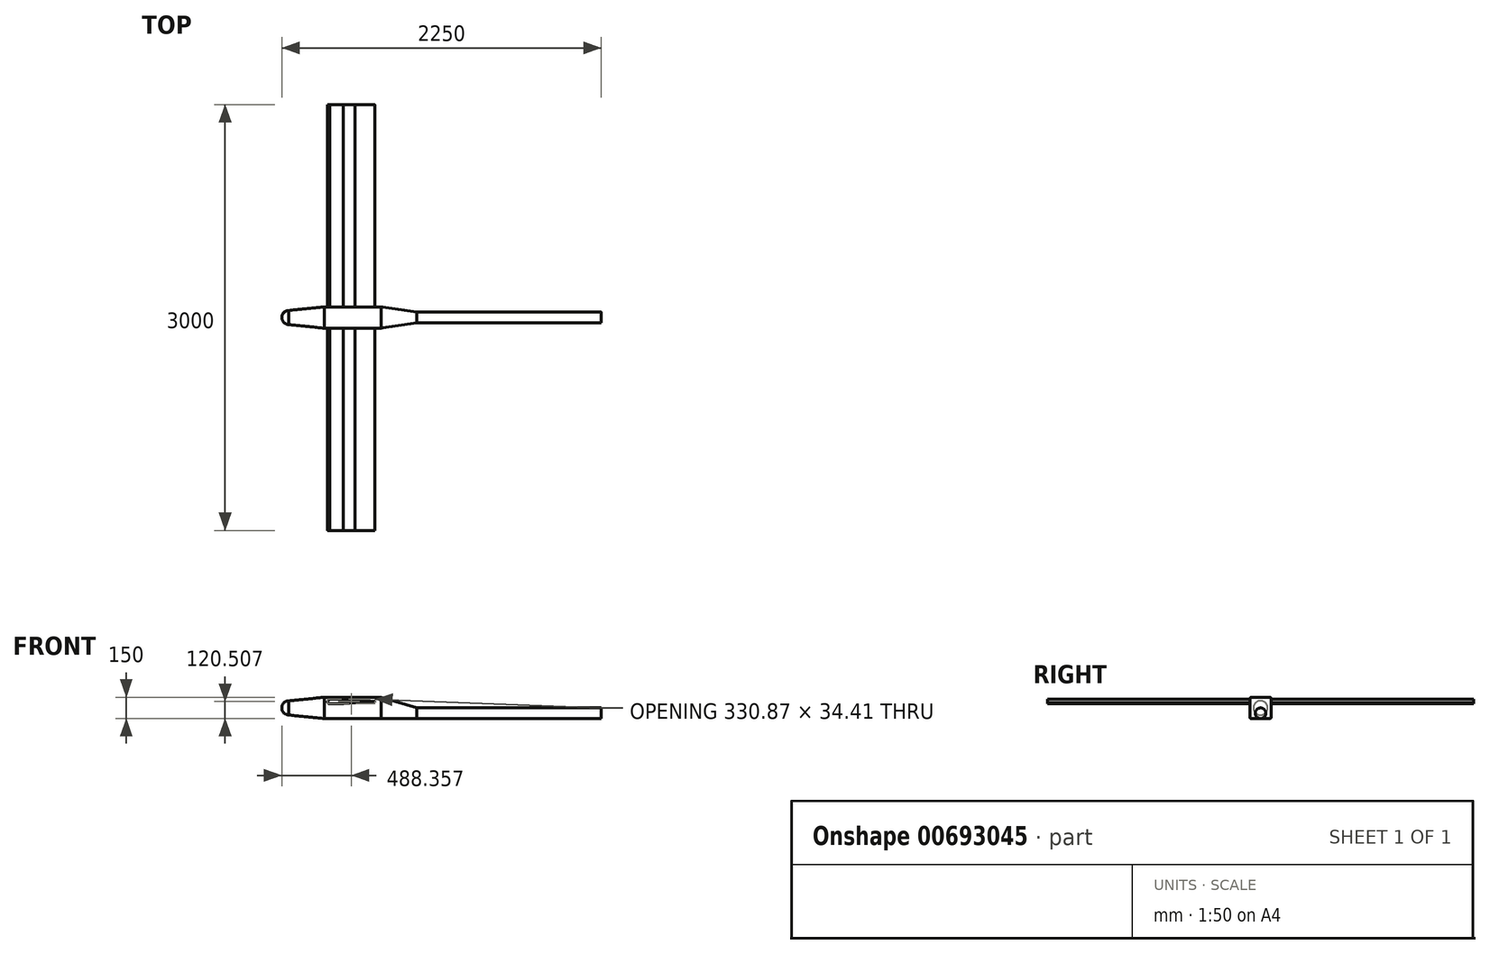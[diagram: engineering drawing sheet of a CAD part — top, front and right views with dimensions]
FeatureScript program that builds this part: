
annotation { "Feature Type Name" : "Feature", "Feature Type Description" : "" }
export const myFeature = defineFeature(function(context is Context, id is Id, definition is map)
    precondition{}
    {
        {
            var Q0;
            Q0=qCreatedBy(makeId("Top.planeOp"),FACE);
            var sketch = newSketch(context, id + "F0", { "sketchPlane" : qUnion([Q0])});
            skLineSegment(sketch, "E0", {"start": v(0, 0) * mm, "end": v(50, 0) * mm, "construction": true});
            skLineSegment(sketch, "E1", {"start": v(0, 0) * mm, "end": v(2000, 0) * mm, "construction": true});
            skCircle(sketch, "E2", {"center": v(50, 0) * mm, "radius": 50 * mm});
            skLineSegment(sketch, "E3", {"start": v(0, 0) * mm, "end": v(300, 0) * mm, "construction": true});
            skLineSegment(sketch, "E4", {"start": v(300, 0) * mm, "end": v(300, -100) * mm, "construction": true});
            skLineSegment(sketch, "E5", {"start": v(300, 0) * mm, "end": v(300, 100) * mm, "construction": true});
            skSolve(sketch);
        }
        {
            var Q0;
            Q0=qCreatedBy(makeId("Right.planeOp"),FACE);
            cPlane(context, id + "F1", {"entities" : qUnion([Q0]), "cplaneType" : CPlaneType.OFFSET, "offset" : 300 * mm, "width" : 152.4 * mm, "height" : 152.4 * mm});
        }
        {
            var Q0;
            Q0=qCreatedBy(makeId("Right.planeOp"),FACE);
            cPlane(context, id + "F2", {"entities" : qUnion([Q0]), "cplaneType" : CPlaneType.OFFSET, "offset" : 50 * mm, "width" : 152.4 * mm, "height" : 152.4 * mm});
        }
        {
            var Q0;
            Q0=qCreatedBy(id+"F2.planeOp",FACE);
            var sketch = newSketch(context, id + "F3", { "sketchPlane" : qUnion([Q0])});
            skCircle(sketch, "E6", {"center": v(0, 0) * mm, "radius": 50 * mm});
            skSolve(sketch);
        }
        {
            var Q0;
            Q0=qCreatedBy(id+"F1.planeOp",FACE);
            var sketch = newSketch(context, id + "F4", { "sketchPlane" : qUnion([Q0])});
            skLineSegment(sketch, "E7.bottom", {"start": v(-65, 75) * mm, "end": v(65, 75) * mm});
            skLineSegment(sketch, "E7.top", {"start": v(-65, -75) * mm, "end": v(65, -75) * mm});
            skLineSegment(sketch, "E7.left", {"start": v(-75, 65) * mm, "end": v(-75, -65) * mm});
            skLineSegment(sketch, "E7.right", {"start": v(75, 65) * mm, "end": v(75, -65) * mm});
            skPoint(sketch, "E7.middle", {"position": v(0, 0) * mm});
            skArc(sketch, "E8", {"start": v(75, 65) * mm, "mid": v(72.07, 72.07) * mm, "end": v(65, 75) * mm});
            skPoint(sketch, "E8.first.point", {"position": v(75, 65) * mm});
            skPoint(sketch, "E8.second.point", {"position": v(65, 75) * mm});
            skPoint(sketch, "E8.third.point", {"position": v(55.59, 61.62) * mm});
            skArc(sketch, "E9", {"start": v(-65, 75) * mm, "mid": v(-72.07, 72.07) * mm, "end": v(-75, 65) * mm});
            skPoint(sketch, "E9.first.point", {"position": v(-65, 75) * mm});
            skPoint(sketch, "E9.second.point", {"position": v(-75, 65) * mm});
            skPoint(sketch, "E9.third.point", {"position": v(-56.26, 60.14) * mm});
            skArc(sketch, "E10", {"start": v(-75, -65) * mm, "mid": v(-72.07, -72.07) * mm, "end": v(-65, -75) * mm});
            skPoint(sketch, "E10.first.point", {"position": v(-75, -65) * mm});
            skPoint(sketch, "E10.second.point", {"position": v(-65, -75) * mm});
            skPoint(sketch, "E10.third.point", {"position": v(-55.94, -69.23) * mm});
            skArc(sketch, "E11", {"start": v(65, -75) * mm, "mid": v(72.07, -72.07) * mm, "end": v(75, -65) * mm});
            skPoint(sketch, "E11.first.point", {"position": v(65, -75) * mm});
            skPoint(sketch, "E11.second.point", {"position": v(75, -65) * mm});
            skPoint(sketch, "E11.third.point", {"position": v(57.58, -58.3) * mm});
            skPoint(sketch, "E12.orphan", {"position": v(75, 75) * mm});
            skPoint(sketch, "E13.orphan", {"position": v(-75, 75) * mm});
            skPoint(sketch, "E14.orphan", {"position": v(75, -75) * mm});
            skPoint(sketch, "E15.orphan", {"position": v(-75, -75) * mm});
            skSolve(sketch);
        }
        {
            var Q0;
            Q0=makeQuery(id+"F4.imprint","IMPRINT",FACE,{"disambiguationData":[TD([[makeQuery(id+"F4.imprint","IMPRINT",EDGE,{"derivedFrom":sQuery(id+"F4.wireOp",EDGE,"E7.bottom")}),-1.0]])]});
            var Q1;
            Q1=makeQuery(id+"F3.imprint","IMPRINT",FACE,{"disambiguationData":[TD([[makeQuery(id+"F3.imprint","IMPRINT",EDGE,{"derivedFrom":sQuery(id+"F3.wireOp",EDGE,"E6")}),1.0]])]});
            loft(context, id + "F5", {"sheetProfilesArray" : [{ "sheetProfileEntities" : qUnion([Q0]) }, { "sheetProfileEntities" : qUnion([Q1]) }]});
        }
        {
            var Q0;
            Q0=qCreatedBy(makeId("Top.planeOp"),FACE);
            var sketch = newSketch(context, id + "F6", { "sketchPlane" : qUnion([Q0])});
            skArc(sketch, "E16", {"start": v(50, 50) * mm, "mid": v(14.64, 35.36) * mm, "end": v(0, 0) * mm});
            skLineSegment(sketch, "E17", {"start": v(50, 0) * mm, "end": v(50, 50) * mm});
            skLineSegment(sketch, "E18", {"start": v(50, 0) * mm, "end": v(0, 0) * mm});
            skSolve(sketch);
        }
        {
            var Q0;
            Q0=makeQuery(id+"F6.imprint","IMPRINT",FACE,{"disambiguationData":[TD([[makeQuery(id+"F6.imprint","IMPRINT",EDGE,{"derivedFrom":sQuery(id+"F6.wireOp",EDGE,"E16")}),1.0]])]});
            var Q1;
            Q1=sQuery(id+"F6.wireOp",EDGE,"E18");
            revolve(context, id + "F7", {"entities" : qUnion([Q0]), "axis" : qUnion([Q1]), "revolveType" : RevolveType.FULL});
        }
        {
            var Q0;
            Q0=makeQuery(id+"F5.opLoft","CAP_FACE",FACE,{"disambiguationData":[OSD([makeQuery(id+"F4.imprint","IMPRINT",FACE,{"disambiguationData":[TD([[makeQuery(id+"F4.imprint","IMPRINT",EDGE,{"derivedFrom":sQuery(id+"F4.wireOp",EDGE,"E7.bottom")}),-1.0]])]})])],"isStart":true});
            extrude(context, id + "F8", {"entities" : qUnion([Q0]), "operationType" : NewBodyOperationType.ADD, "depth" : 400 * mm, "offsetDistance" : 25.4 * mm});
        }
        {
            var Q0;
            Q0=qCreatedBy(makeId("Right.planeOp"),FACE);
            cPlane(context, id + "F9", {"entities" : qUnion([Q0]), "cplaneType" : CPlaneType.OFFSET, "offset" : 950 * mm, "width" : 152.4 * mm, "height" : 152.4 * mm});
        }
        {
            var Q0;
            Q0=qCreatedBy(id+"F9.planeOp",FACE);
            var sketch = newSketch(context, id + "F10", { "sketchPlane" : qUnion([Q0])});
            skLineSegment(sketch, "E19", {"start": v(0, 0) * mm, "end": v(0, -75) * mm, "construction": true});
            skCircle(sketch, "E20", {"center": v(0, -37.5) * mm, "radius": 37.5 * mm});
            skPoint(sketch, "E20.third.point", {"position": v(35.6, -49.3) * mm});
            skSolve(sketch);
        }
        {
            var Q1;
            Q1=makeQuery(id+"F8.opExtrude","CAP_FACE",FACE,{"disambiguationData":[OSD([makeQuery(id+"F4.imprint","IMPRINT",FACE,{"disambiguationData":[TD([[makeQuery(id+"F4.imprint","IMPRINT",EDGE,{"derivedFrom":sQuery(id+"F4.wireOp",EDGE,"E7.bottom")}),-1.0]])]})])],"isStart":false});
            var Q2;
            Q2=makeQuery(id+"F10.imprint","IMPRINT",FACE,{"disambiguationData":[TD([[makeQuery(id+"F10.imprint","IMPRINT",EDGE,{"derivedFrom":sQuery(id+"F10.wireOp",EDGE,"E20")}),1.0]])]});
            loft(context, id + "F11", {"operationType" : NewBodyOperationType.ADD, "sheetProfilesArray" : [{ "sheetProfileEntities" : qUnion([Q1]) }, { "sheetProfileEntities" : qUnion([Q2]) }]});
        }
        {
            var Q0;
            Q0=makeQuery(id+"F11.opLoft","CAP_FACE",FACE,{"disambiguationData":[OSD([makeQuery(id+"F10.imprint","IMPRINT",FACE,{"disambiguationData":[TD([[makeQuery(id+"F10.imprint","IMPRINT",EDGE,{"derivedFrom":sQuery(id+"F10.wireOp",EDGE,"E20")}),1.0]])]})])],"isStart":true});
            extrude(context, id + "F12", {"entities" : qUnion([Q0]), "operationType" : NewBodyOperationType.ADD, "depth" : 1050 * mm, "offsetDistance" : 25.4 * mm});
        }
        {
            var Q0;
            Q0=qCreatedBy(makeId("Front.planeOp"),FACE);
            var sketch = newSketch(context, id + "F13", { "sketchPlane" : qUnion([Q0])});
            skArc(sketch, "E21", {"start": v(337.32, 57.09) * mm, "mid": v(322.92, 42.28) * mm, "end": v(338.14, 28.3) * mm});
            skPoint(sketch, "E21.first.point", {"position": v(350.32, 48.9) * mm});
            skPoint(sketch, "E21.second.point", {"position": v(325.99, 33.8) * mm});
            skPoint(sketch, "E21.third.point", {"position": v(346.12, 31.28) * mm});
            skArc(sketch, "E22", {"start": v(434.06, 31.02) * mm, "mid": v(434.91, 31.05) * mm, "end": v(435.77, 31.13) * mm});
            skPoint(sketch, "E22.first.point", {"position": v(441.77, 60.65) * mm});
            skPoint(sketch, "E22.second.point", {"position": v(424.99, 33.8) * mm});
            skPoint(sketch, "E22.third.point", {"position": v(449.32, 43.03) * mm});
            skPoint(sketch, "E23.first.point", {"position": v(525.67, 53.93) * mm});
            skPoint(sketch, "E23.second.point", {"position": v(504.7, 38.83) * mm});
            skPoint(sketch, "E23.third.point", {"position": v(521.47, 38.83) * mm});
            skArc(sketch, "E24", {"start": v(651.54, 41.49) * mm, "mid": v(653.8, 43.74) * mm, "end": v(651.73, 46.16) * mm});
            skPoint(sketch, "E24.first.point", {"position": v(653.8, 43.83) * mm});
            skPoint(sketch, "E24.second.point", {"position": v(651.54, 41.49) * mm});
            skPoint(sketch, "E24.third.point", {"position": v(650.15, 45.8) * mm});
            skPoint(sketch, "E25.end.orphan", {"position": v(659.48, 45.8) * mm});
            skLineSegment(sketch, "E26", {"start": v(651.73, 46.16) * mm, "end": v(514.66, 62.71) * mm});
            skLineSegment(sketch, "E27", {"start": v(514.66, 62.71) * mm, "end": v(433.95, 62.71) * mm});
            skLineSegment(sketch, "E28", {"start": v(433.95, 62.71) * mm, "end": v(337.32, 57.11) * mm});
            skLineSegment(sketch, "E29", {"start": v(337.32, 57.11) * mm, "end": v(337.32, 57.09) * mm});
            skLineSegment(sketch, "E30", {"start": v(337.32, 28.28) * mm, "end": v(433.95, 31.02) * mm});
            skLineSegment(sketch, "E31", {"start": v(433.95, 31.02) * mm, "end": v(519.09, 36.23) * mm});
            skLineSegment(sketch, "E32", {"start": v(519.09, 36.23) * mm, "end": v(651.54, 41.49) * mm});
            skPoint(sketch, "E23.center.orphan", {"position": v(513.08, 49.3) * mm});
            skLineSegment(sketch, "E33.trimOffspring", {"start": v(433.95, 62.71) * mm, "end": v(433.95, 62.71) * mm});
            skSolve(sketch);
        }
        {
            var Q0;
            Q0 = qSketchRegion(id + "F13", true);
            extrude(context, id + "F14", {"entities" : qUnion([Q0]), "operationType" : NewBodyOperationType.ADD, "depth" : 1500 * mm, "offsetDistance" : 25.4 * mm, "hasSecondDirection" : true, "secondDirectionOppositeDirection" : true, "secondDirectionDepth" : 1500 * mm});
        }
        {
            var Q0;
            Q0=makeQuery(id+"F12.opExtrude","CAP_FACE",FACE,{"disambiguationData":[OSD([makeQuery(id+"F10.imprint","IMPRINT",FACE,{"disambiguationData":[TD([[makeQuery(id+"F10.imprint","IMPRINT",EDGE,{"derivedFrom":sQuery(id+"F10.wireOp",EDGE,"E20")}),1.0]])]})])],"isStart":false});
            extrude(context, id + "F15", {"entities" : qUnion([Q0]), "operationType" : NewBodyOperationType.ADD, "depth" : 250 * mm, "offsetDistance" : 25.4 * mm});
        }
    });
